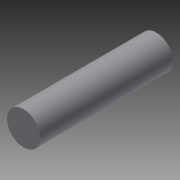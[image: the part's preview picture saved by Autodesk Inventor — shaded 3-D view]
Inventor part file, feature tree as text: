
AUTODESK INVENTOR PART (.ipt)
format: ipt  version: 2014 (Build 180170000, 170)  size: 70,144 bytes
history: native  units: in
note: dims shown in document units (in); Inventor stores cm internally (conversion verified against a paired STEP export)
features: extrude x1, sketch x1
ambient origin geometry x8: Origin, YZ Plane, XZ Plane, XY Plane, X Axis, Y Axis, Z Axis, Center Point
bodies: Solid1 (feature_tree)
feature tree (2):
  extrude  "Extrusion1"  Depth=2.0in TaperAngle=0.0deg
  sketch  "Sketch1"  dims[d0=0.5in d1=2.0in d2=0.0in]
